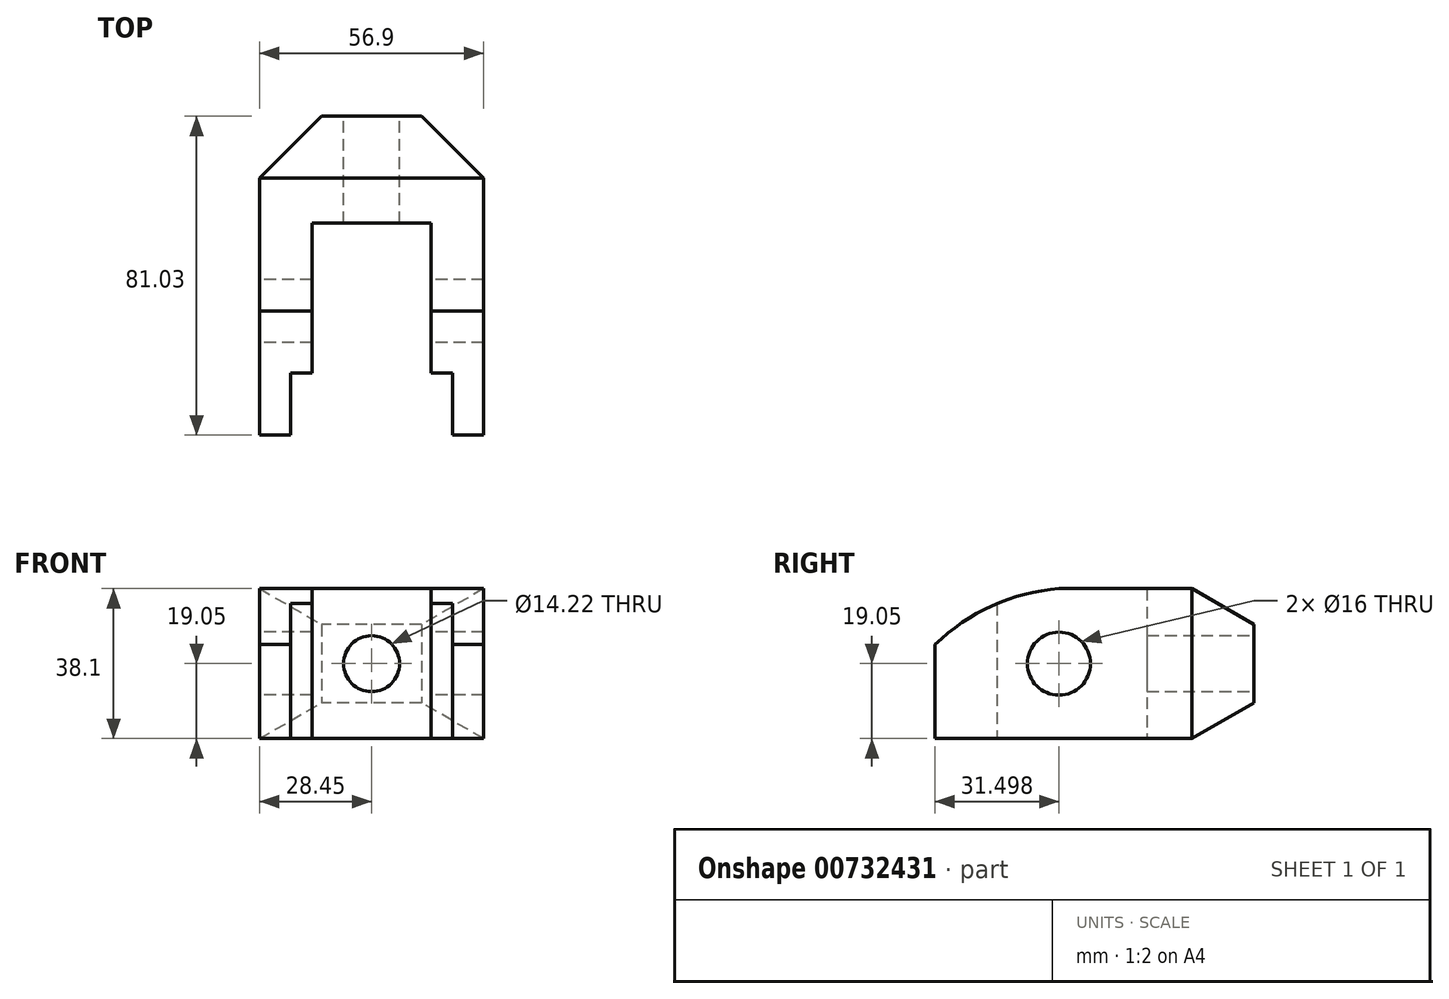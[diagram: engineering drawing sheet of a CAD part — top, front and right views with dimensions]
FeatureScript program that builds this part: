
annotation { "Feature Type Name" : "Feature", "Feature Type Description" : "" }
export const myFeature = defineFeature(function(context is Context, id is Id, definition is map)
    precondition{}
    {
        {
            var Q0;
            Q0=qCreatedBy(makeId("Top.planeOp"),FACE);
            var sketch = newSketch(context, id + "F0", { "sketchPlane" : qUnion([Q0])});
            skLineSegment(sketch, "E0", {"start": v(0, 0) * mm, "end": v(-15.11, 0) * mm});
            skLineSegment(sketch, "E1", {"start": v(-15.11, 0) * mm, "end": v(-15.11, -38.1) * mm});
            skLineSegment(sketch, "E2", {"start": v(-15.11, -38.1) * mm, "end": v(-20.57, -38.1) * mm});
            skLineSegment(sketch, "E3", {"start": v(-20.57, -38.1) * mm, "end": v(-20.57, -53.85) * mm});
            skLineSegment(sketch, "E4", {"start": v(-20.57, -53.85) * mm, "end": v(-28.45, -53.85) * mm});
            skLineSegment(sketch, "E5", {"start": v(-28.45, -53.85) * mm, "end": v(-28.45, 11.43) * mm});
            skLineSegment(sketch, "E6", {"start": v(-28.45, 11.43) * mm, "end": v(-12.7, 27.18) * mm});
            skLineSegment(sketch, "E7", {"start": v(-12.7, 27.18) * mm, "end": v(0, 27.18) * mm});
            skLineSegment(sketch, "E8.MirrorCS", {"start": v(20.57, -53.85) * mm, "end": v(28.45, -53.85) * mm});
            skLineSegment(sketch, "E9.MirrorCS", {"start": v(20.57, -38.1) * mm, "end": v(20.57, -53.85) * mm});
            skLineSegment(sketch, "E10.MirrorCS", {"start": v(15.11, -38.1) * mm, "end": v(20.57, -38.1) * mm});
            skLineSegment(sketch, "E11.MirrorCS", {"start": v(15.11, 0) * mm, "end": v(15.11, -38.1) * mm});
            skLineSegment(sketch, "E12.MirrorCS", {"start": v(0, 0) * mm, "end": v(15.11, 0) * mm});
            skLineSegment(sketch, "E13.MirrorCS", {"start": v(28.45, -53.85) * mm, "end": v(28.45, 11.43) * mm});
            skLineSegment(sketch, "E14.MirrorCS", {"start": v(12.7, 27.18) * mm, "end": v(0, 27.18) * mm});
            skLineSegment(sketch, "E15.MirrorCS", {"start": v(28.45, 11.43) * mm, "end": v(12.7, 27.18) * mm});
            skSolve(sketch);
        }
        {
            var Q0;
            Q0=makeQuery(id+"F0.imprint","IMPRINT",FACE,{"disambiguationData":[TD([[makeQuery(id+"F0.imprint","IMPRINT",EDGE,{"derivedFrom":sQuery(id+"F0.wireOp",EDGE,"E0")}),-1.0]])]});
            extrude(context, id + "F1", {"entities" : qUnion([Q0]), "depth" : 38.1 * mm, "offsetDistance" : 25.4 * mm});
        }
        {
            var Q0;
            Q0=qCreatedBy(makeId("Right.planeOp"),FACE);
            var sketch = newSketch(context, id + "F2", { "sketchPlane" : qUnion([Q0])});
            skLineSegment(sketch, "E16.0", {"start": v(11.43, 38.1) * mm, "end": v(27.18, 38.1) * mm});
            skLineSegment(sketch, "E17.0", {"start": v(11.43, 0) * mm, "end": v(27.18, 0) * mm});
            skLineSegment(sketch, "E18", {"start": v(11.43, 0) * mm, "end": v(27.18, 9.1) * mm});
            skLineSegment(sketch, "E19", {"start": v(11.43, 38.1) * mm, "end": v(27.18, 29) * mm});
            skLineSegment(sketch, "E20.trimOffspring", {"start": v(27.18, 9.1) * mm, "end": v(27.18, 0) * mm});
            skLineSegment(sketch, "E21", {"start": v(27.18, 38.1) * mm, "end": v(27.18, 29) * mm});
            skSolve(sketch);
        }
        {
            var Q0;
            Q0 = qSketchRegion(id + "F2", true);
            extrude(context, id + "F3", {"entities" : qUnion([Q0]), "operationType" : NewBodyOperationType.REMOVE, "endBound" : BoundingType.SYMMETRIC, "depth" : 56.9 * mm, "offsetDistance" : 25.4 * mm});
        }
        {
            var Q0;
            Q0=makeQuery(id+"F1.opExtrude","SWEPT_FACE",FACE,{"disambiguationData":[OSD([sQuery(id+"F0.wireOp",EDGE,"E7"),sQuery(id+"F0.wireOp",EDGE,"E14.MirrorCS")])]});
            var sketch = newSketch(context, id + "F4", { "sketchPlane" : qUnion([Q0])});
            skCircle(sketch, "E22", {"center": v(0, 19.05) * mm, "radius": 7.11 * mm});
            skPoint(sketch, "E22.centerSnap0", {"position": v(12.7, 19.05) * mm});
            skSolve(sketch);
        }
        {
            var Q0;
            Q0 = qSketchRegion(id + "F4", true);
            extrude(context, id + "F5", {"entities" : qUnion([Q0]), "operationType" : NewBodyOperationType.REMOVE, "oppositeDirection" : true, "depth" : 27.18 * mm, "offsetDistance" : 25.4 * mm});
        }
        {
            var Q0;
            Q0=qCreatedBy(makeId("Right.planeOp"),FACE);
            var sketch = newSketch(context, id + "F6", { "sketchPlane" : qUnion([Q0])});
            skCircle(sketch, "E23", {"center": v(-22.35, 19.05) * mm, "radius": 8 * mm});
            skLineSegment(sketch, "E24", {"start": v(-71.76, 23.88) * mm, "end": v(-43.32, 23.88) * mm, "construction": true});
            skLineSegment(sketch, "E25", {"start": v(-22.35, 19.05) * mm, "end": v(-22.35, 48.06) * mm, "construction": true});
            skPoint(sketch, "E26", {"position": v(-53.85, 23.88) * mm});
            skPoint(sketch, "E27", {"position": v(-22.35, 38.1) * mm});
            skArc(sketch, "E28", {"start": v(-22.35, 38.1) * mm, "mid": v(-39.35, 33.75) * mm, "end": v(-53.85, 23.88) * mm});
            skLineSegment(sketch, "E29", {"start": v(-22.35, 38.1) * mm, "end": v(-53.85, 38.1) * mm});
            skLineSegment(sketch, "E30", {"start": v(-53.85, 23.88) * mm, "end": v(-53.85, 38.1) * mm});
            skSolve(sketch);
        }
        {
            var Q0;
            Q0 = qSketchRegion(id + "F6", true);
            extrude(context, id + "F7", {"entities" : qUnion([Q0]), "operationType" : NewBodyOperationType.REMOVE, "endBound" : BoundingType.SYMMETRIC, "depth" : 56.9 * mm, "offsetDistance" : 25.4 * mm});
        }
    });
